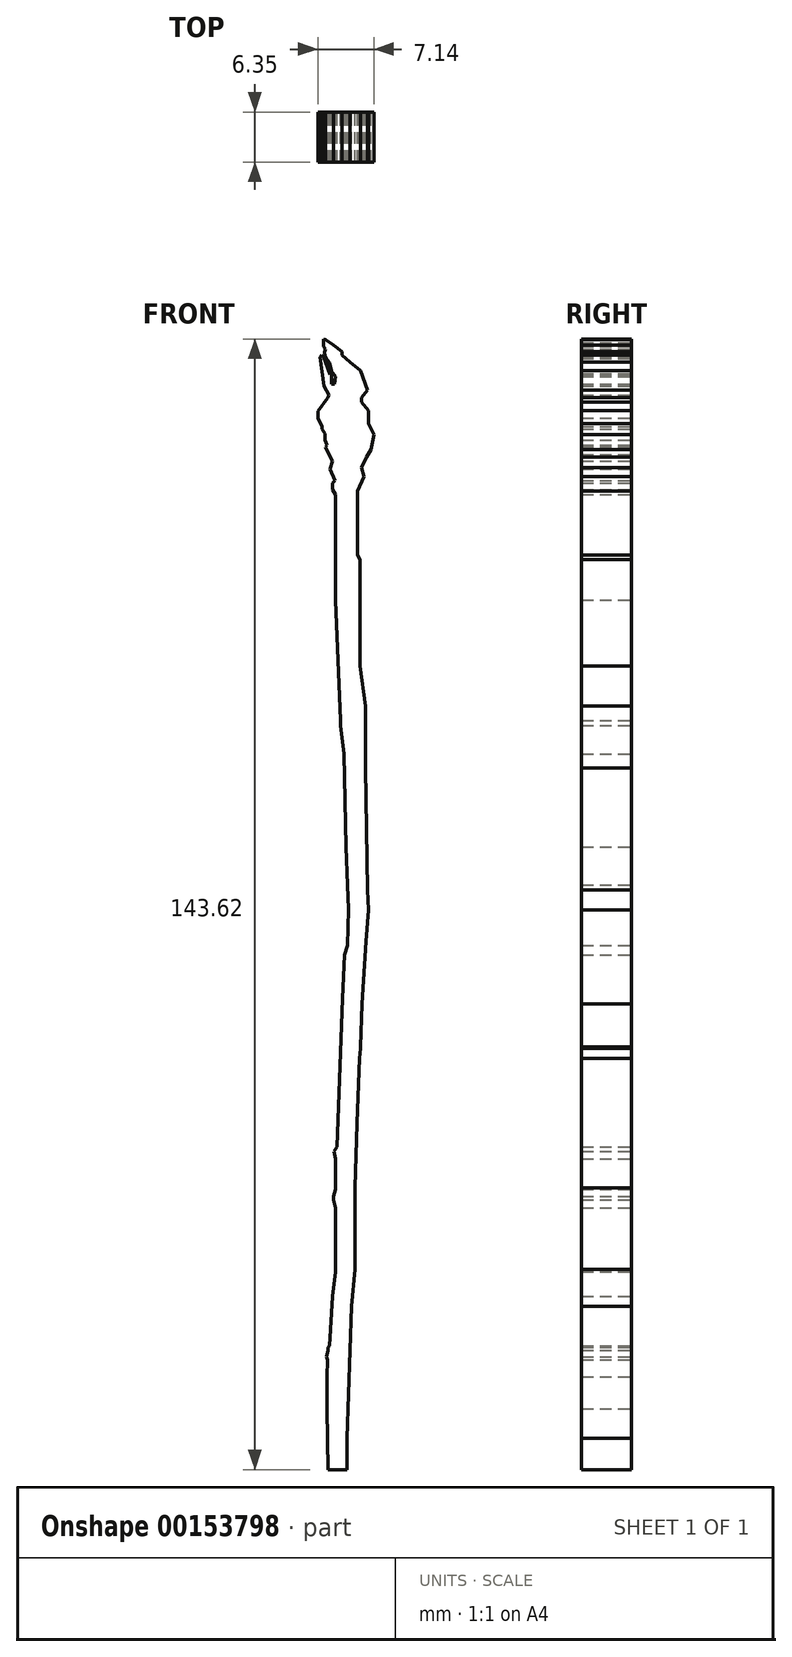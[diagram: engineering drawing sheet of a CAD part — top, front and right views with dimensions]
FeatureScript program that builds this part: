
annotation { "Feature Type Name" : "Feature", "Feature Type Description" : "" }
export const myFeature = defineFeature(function(context is Context, id is Id, definition is map)
    precondition{}
    {
        {
            var Q0;
            Q0=qCreatedBy(makeId("Front.planeOp"),FACE);
            var sketch = newSketch(context, id + "F0", { "sketchPlane" : qUnion([Q0])});
            skLineSegment(sketch, "E0", {"start": v(-59.72, 71.34) * mm, "end": v(-58.68, 70.68) * mm});
            skLineSegment(sketch, "E1", {"start": v(-58.68, 70.68) * mm, "end": v(-57.64, 69.82) * mm});
            skLineSegment(sketch, "E2", {"start": v(-57.64, 69.82) * mm, "end": v(-57.64, 69.37) * mm});
            skLineSegment(sketch, "E3", {"start": v(-57.64, 69.37) * mm, "end": v(-56.6, 68.48) * mm});
            skLineSegment(sketch, "E4", {"start": v(-56.6, 68.48) * mm, "end": v(-55.3, 67.4) * mm});
            skLineSegment(sketch, "E5", {"start": v(-55.3, 67.4) * mm, "end": v(-54.4, 64.91) * mm});
            skLineSegment(sketch, "E6", {"start": v(-54.4, 64.91) * mm, "end": v(-55.1, 64.02) * mm});
            skLineSegment(sketch, "E7", {"start": v(-55.1, 64.02) * mm, "end": v(-55.1, 63.4) * mm});
            skLineSegment(sketch, "E8", {"start": v(-55.1, 63.4) * mm, "end": v(-54.25, 62.35) * mm});
            skLineSegment(sketch, "E9", {"start": v(-54.25, 62.35) * mm, "end": v(-54.25, 61.01) * mm});
            skLineSegment(sketch, "E10", {"start": v(-54.25, 61.01) * mm, "end": v(-54.25, 60.72) * mm});
            skLineSegment(sketch, "E11", {"start": v(-54.25, 60.72) * mm, "end": v(-53.55, 59.3) * mm});
            skLineSegment(sketch, "E12", {"start": v(-53.55, 59.3) * mm, "end": v(-53.96, 57.37) * mm});
            skLineSegment(sketch, "E13", {"start": v(-53.96, 57.37) * mm, "end": v(-54.51, 56.44) * mm});
            skLineSegment(sketch, "E14", {"start": v(-54.51, 56.44) * mm, "end": v(-55.1, 55.1) * mm});
            skLineSegment(sketch, "E15", {"start": v(-55.1, 55.1) * mm, "end": v(-54.81, 53.95) * mm});
            skLineSegment(sketch, "E16", {"start": v(-54.81, 53.95) * mm, "end": v(-55.63, 52.1) * mm});
            skLineSegment(sketch, "E17", {"start": v(-55.63, 52.1) * mm, "end": v(-55.63, 50.94) * mm});
            skLineSegment(sketch, "E18", {"start": v(-55.63, 50.94) * mm, "end": v(-55.63, 44) * mm});
            skLineSegment(sketch, "E19", {"start": v(-55.63, 44) * mm, "end": v(-55.33, 43.4) * mm});
            skLineSegment(sketch, "E20", {"start": v(-55.33, 43.4) * mm, "end": v(-55.33, 34.03) * mm});
            skLineSegment(sketch, "E21", {"start": v(-55.33, 34.03) * mm, "end": v(-55.33, 29.92) * mm});
            skLineSegment(sketch, "E22", {"start": v(-55.33, 29.92) * mm, "end": v(-54.65, 24.82) * mm});
            skLineSegment(sketch, "E23", {"start": v(-54.65, 24.82) * mm, "end": v(-54.65, 16.96) * mm});
            skLineSegment(sketch, "E24", {"start": v(-54.65, 16.96) * mm, "end": v(-54.4, 1.47) * mm});
            skLineSegment(sketch, "E25", {"start": v(-54.4, 1.47) * mm, "end": v(-54.28, -1.09) * mm});
            skLineSegment(sketch, "E26", {"start": v(-54.28, -1.09) * mm, "end": v(-54.54, -5.08) * mm});
            skLineSegment(sketch, "E27", {"start": v(-54.54, -5.08) * mm, "end": v(-55.1, -13.06) * mm});
            skLineSegment(sketch, "E28", {"start": v(-55.1, -13.06) * mm, "end": v(-55.27, -18.5) * mm});
            skLineSegment(sketch, "E29", {"start": v(-55.27, -18.5) * mm, "end": v(-55.27, -18.7) * mm});
            skLineSegment(sketch, "E30", {"start": v(-55.27, -18.7) * mm, "end": v(-55.41, -19.94) * mm});
            skLineSegment(sketch, "E31", {"start": v(-55.41, -19.94) * mm, "end": v(-55.51, -23.2) * mm});
            skLineSegment(sketch, "E32", {"start": v(-55.51, -23.2) * mm, "end": v(-55.72, -28.22) * mm});
            skLineSegment(sketch, "E33", {"start": v(-55.72, -28.22) * mm, "end": v(-55.99, -36.42) * mm});
            skLineSegment(sketch, "E34", {"start": v(-55.99, -36.42) * mm, "end": v(-55.99, -46.78) * mm});
            skLineSegment(sketch, "E35", {"start": v(-55.99, -46.78) * mm, "end": v(-56.43, -51.44) * mm});
            skLineSegment(sketch, "E36", {"start": v(-56.43, -51.44) * mm, "end": v(-57, -68.19) * mm});
            skLineSegment(sketch, "E37", {"start": v(-57, -68.19) * mm, "end": v(-57, -71.95) * mm});
            skLineSegment(sketch, "E38", {"start": v(-57, -71.95) * mm, "end": v(-57, -72.19) * mm});
            skLineSegment(sketch, "E39", {"start": v(-57, -72.19) * mm, "end": v(-59.38, -72.19) * mm});
            skLineSegment(sketch, "E40", {"start": v(-59.38, -72.19) * mm, "end": v(-59.53, -64.49) * mm});
            skLineSegment(sketch, "E41", {"start": v(-59.53, -64.49) * mm, "end": v(-59.53, -60.39) * mm});
            skLineSegment(sketch, "E42", {"start": v(-59.53, -60.39) * mm, "end": v(-59.44, -58.26) * mm});
            skLineSegment(sketch, "E43", {"start": v(-59.44, -58.26) * mm, "end": v(-59.6, -57.9) * mm});
            skLineSegment(sketch, "E44", {"start": v(-59.6, -57.9) * mm, "end": v(-59.37, -57.04) * mm});
            skLineSegment(sketch, "E45", {"start": v(-59.37, -57.04) * mm, "end": v(-59.37, -56.65) * mm});
            skLineSegment(sketch, "E46", {"start": v(-59.37, -56.65) * mm, "end": v(-59.2, -56.48) * mm});
            skLineSegment(sketch, "E47", {"start": v(-59.2, -56.48) * mm, "end": v(-58.85, -50.2) * mm});
            skLineSegment(sketch, "E48", {"start": v(-58.85, -50.2) * mm, "end": v(-58.46, -47.07) * mm});
            skLineSegment(sketch, "E49", {"start": v(-58.46, -47.07) * mm, "end": v(-58.46, -38.92) * mm});
            skLineSegment(sketch, "E50", {"start": v(-58.46, -38.92) * mm, "end": v(-58.7, -37.9) * mm});
            skLineSegment(sketch, "E51", {"start": v(-58.7, -37.9) * mm, "end": v(-58.7, -37.45) * mm});
            skLineSegment(sketch, "E52", {"start": v(-58.7, -37.45) * mm, "end": v(-58.42, -36.6) * mm});
            skLineSegment(sketch, "E53", {"start": v(-58.42, -36.6) * mm, "end": v(-58.42, -32.7) * mm});
            skLineSegment(sketch, "E54", {"start": v(-58.42, -32.7) * mm, "end": v(-58.64, -31.78) * mm});
            skLineSegment(sketch, "E55", {"start": v(-58.64, -31.78) * mm, "end": v(-58.27, -31.22) * mm});
            skLineSegment(sketch, "E56", {"start": v(-58.27, -31.22) * mm, "end": v(-57.53, -12.33) * mm});
            skLineSegment(sketch, "E57", {"start": v(-57.53, -12.33) * mm, "end": v(-57.3, -6.82) * mm});
            skLineSegment(sketch, "E58", {"start": v(-57.3, -6.82) * mm, "end": v(-56.94, -5.6) * mm});
            skLineSegment(sketch, "E59", {"start": v(-56.94, -5.6) * mm, "end": v(-56.76, -1.03) * mm});
            skLineSegment(sketch, "E60", {"start": v(-56.76, -1.03) * mm, "end": v(-56.94, 2.06) * mm});
            skLineSegment(sketch, "E61", {"start": v(-56.94, 2.06) * mm, "end": v(-57.13, 6.93) * mm});
            skLineSegment(sketch, "E62", {"start": v(-57.13, 6.93) * mm, "end": v(-57.33, 18.7) * mm});
            skLineSegment(sketch, "E63", {"start": v(-57.33, 18.7) * mm, "end": v(-57.8, 22.31) * mm});
            skLineSegment(sketch, "E64", {"start": v(-57.8, 22.31) * mm, "end": v(-57.8, 22.98) * mm});
            skLineSegment(sketch, "E65", {"start": v(-57.8, 22.98) * mm, "end": v(-58.46, 38.3) * mm});
            skLineSegment(sketch, "E66", {"start": v(-58.46, 38.3) * mm, "end": v(-58.46, 43.55) * mm});
            skLineSegment(sketch, "E67", {"start": v(-58.46, 43.55) * mm, "end": v(-58.46, 51.22) * mm});
            skLineSegment(sketch, "E68", {"start": v(-58.46, 51.22) * mm, "end": v(-58.46, 51.66) * mm});
            skLineSegment(sketch, "E69", {"start": v(-58.46, 51.66) * mm, "end": v(-58.8, 52.33) * mm});
            skLineSegment(sketch, "E70", {"start": v(-58.8, 52.33) * mm, "end": v(-58.8, 53.16) * mm});
            skLineSegment(sketch, "E71", {"start": v(-58.8, 53.16) * mm, "end": v(-58.52, 53.43) * mm});
            skLineSegment(sketch, "E72", {"start": v(-58.52, 53.43) * mm, "end": v(-59.13, 54.91) * mm});
            skLineSegment(sketch, "E73", {"start": v(-59.13, 54.91) * mm, "end": v(-58.8, 55.91) * mm});
            skLineSegment(sketch, "E74", {"start": v(-58.8, 55.91) * mm, "end": v(-59.25, 56.77) * mm});
            skLineSegment(sketch, "E75", {"start": v(-59.25, 56.77) * mm, "end": v(-59.69, 57.69) * mm});
            skLineSegment(sketch, "E76", {"start": v(-59.69, 57.69) * mm, "end": v(-59.52, 57.94) * mm});
            skLineSegment(sketch, "E77", {"start": v(-59.52, 57.94) * mm, "end": v(-59.8, 58.6) * mm});
            skLineSegment(sketch, "E78", {"start": v(-59.8, 58.6) * mm, "end": v(-59.8, 59.42) * mm});
            skLineSegment(sketch, "E79", {"start": v(-59.8, 59.42) * mm, "end": v(-60.17, 60) * mm});
            skLineSegment(sketch, "E80", {"start": v(-60.17, 60) * mm, "end": v(-60.17, 60.33) * mm});
            skLineSegment(sketch, "E81", {"start": v(-60.17, 60.33) * mm, "end": v(-60.7, 61.42) * mm});
            skLineSegment(sketch, "E82", {"start": v(-60.7, 61.42) * mm, "end": v(-60.7, 62.3) * mm});
            skLineSegment(sketch, "E83", {"start": v(-60.7, 62.3) * mm, "end": v(-59.48, 63.92) * mm});
            skLineSegment(sketch, "E84", {"start": v(-59.48, 63.92) * mm, "end": v(-59.3, 64.34) * mm});
            skLineSegment(sketch, "E85", {"start": v(-59.3, 64.34) * mm, "end": v(-59.87, 65.46) * mm});
            skLineSegment(sketch, "E86", {"start": v(-59.87, 65.46) * mm, "end": v(-60.43, 69.11) * mm});
            skLineSegment(sketch, "E87", {"start": v(-60.43, 69.11) * mm, "end": v(-60.22, 69.4) * mm});
            skLineSegment(sketch, "E88", {"start": v(-60.22, 69.4) * mm, "end": v(-59.97, 69.2) * mm});
            skLineSegment(sketch, "E89", {"start": v(-59.97, 69.2) * mm, "end": v(-59.13, 66.94) * mm});
            skLineSegment(sketch, "E90", {"start": v(-59.13, 66.94) * mm, "end": v(-58.92, 67.02) * mm});
            skLineSegment(sketch, "E91", {"start": v(-58.92, 67.02) * mm, "end": v(-58.92, 66.64) * mm});
            skLineSegment(sketch, "E92", {"start": v(-58.92, 66.64) * mm, "end": v(-58.92, 65.73) * mm});
            skLineSegment(sketch, "E93", {"start": v(-58.92, 65.73) * mm, "end": v(-58.57, 65.73) * mm});
            skLineSegment(sketch, "E94", {"start": v(-58.57, 65.73) * mm, "end": v(-58.43, 66.7) * mm});
            skLineSegment(sketch, "E95", {"start": v(-58.43, 66.7) * mm, "end": v(-58.94, 67.34) * mm});
            skLineSegment(sketch, "E96", {"start": v(-58.94, 67.34) * mm, "end": v(-59.17, 68.41) * mm});
            skLineSegment(sketch, "E97", {"start": v(-59.17, 68.41) * mm, "end": v(-59.59, 68.97) * mm});
            skLineSegment(sketch, "E98", {"start": v(-59.59, 68.97) * mm, "end": v(-59.8, 69.36) * mm});
            skLineSegment(sketch, "E99", {"start": v(-59.8, 69.36) * mm, "end": v(-59.84, 69.78) * mm});
            skLineSegment(sketch, "E100", {"start": v(-59.84, 69.78) * mm, "end": v(-59.71, 70.13) * mm});
            skLineSegment(sketch, "E101", {"start": v(-59.71, 70.13) * mm, "end": v(-59.94, 70.45) * mm});
            skLineSegment(sketch, "E102", {"start": v(-59.94, 70.45) * mm, "end": v(-59.98, 71) * mm});
            skLineSegment(sketch, "E103", {"start": v(-59.98, 71) * mm, "end": v(-59.98, 71.43) * mm});
            skLineSegment(sketch, "E104", {"start": v(-59.98, 71.43) * mm, "end": v(-59.72, 71.34) * mm});
            skSolve(sketch);
        }
        {
            var Q0;
            Q0 = qSketchRegion(id + "F0", true);
            var Q1;
            Q1=makeQuery(id+"F0.imprint","IMPRINT",FACE,{"disambiguationData":[TD([[makeQuery(id+"F0.imprint","IMPRINT",EDGE,{"derivedFrom":sQuery(id+"F0.wireOp",EDGE,"E0")}),-1.0]])]});
            extrude(context, id + "F1", {"entities" : qUnion([Q0, Q1]), "depth" : 6.35 * mm});
        }
    });
